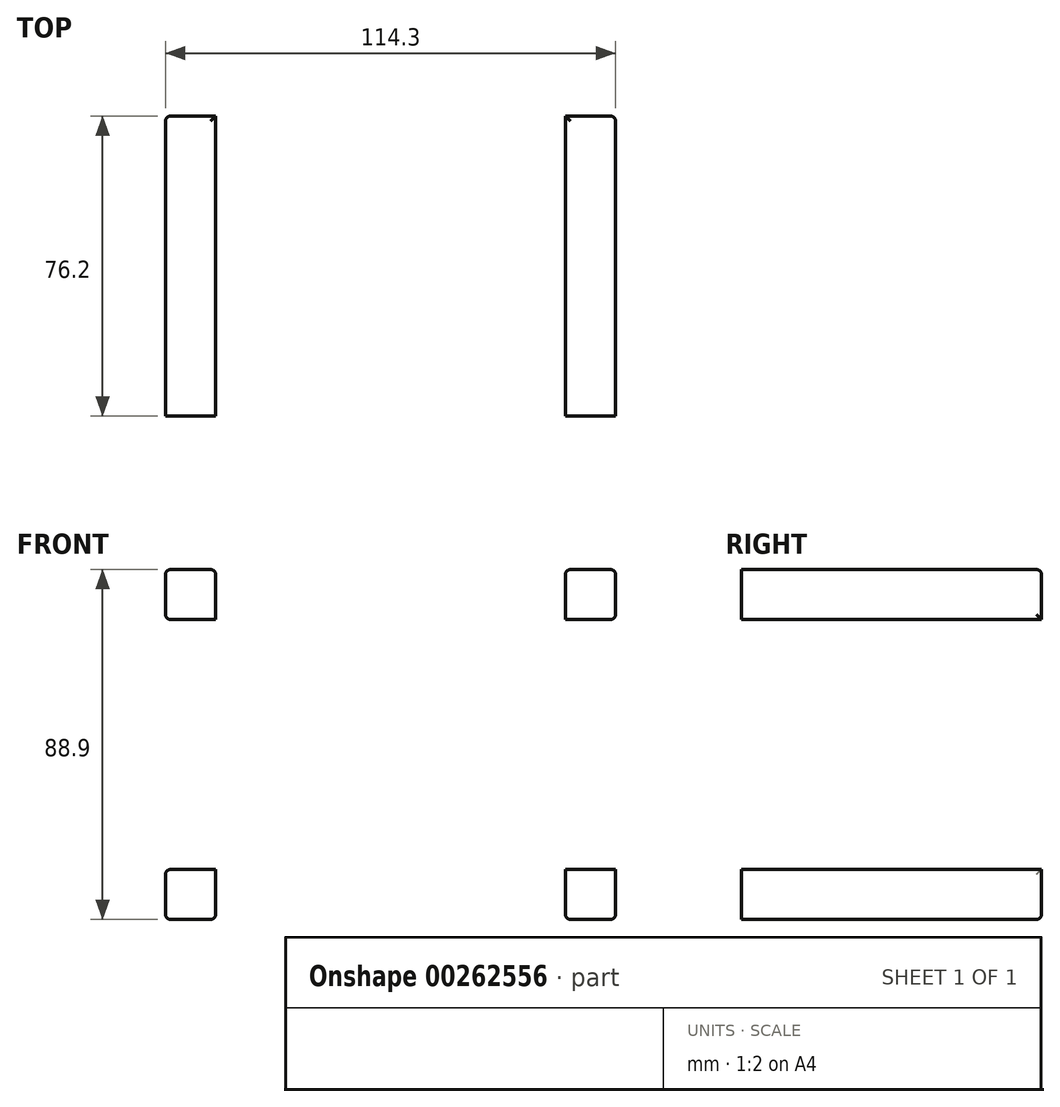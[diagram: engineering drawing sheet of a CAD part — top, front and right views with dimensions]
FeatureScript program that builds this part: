
annotation { "Feature Type Name" : "Feature", "Feature Type Description" : "" }
export const myFeature = defineFeature(function(context is Context, id is Id, definition is map)
    precondition{}
    {
        {
            var Q0;
            Q0=qCreatedBy(makeId("Front.planeOp"),FACE);
            var sketch = newSketch(context, id + "F0", { "sketchPlane" : qUnion([Q0])});
            skPoint(sketch, "E0.middle", {"position": v(0, 0) * mm});
            skLineSegment(sketch, "E1.bottom", {"start": v(-57.15, 44.45) * mm, "end": v(-44.45, 44.45) * mm});
            skLineSegment(sketch, "E1.top", {"start": v(-57.15, 31.75) * mm, "end": v(-44.45, 31.75) * mm});
            skLineSegment(sketch, "E1.left", {"start": v(-57.15, 44.45) * mm, "end": v(-57.15, 31.75) * mm});
            skLineSegment(sketch, "E1.right", {"start": v(-44.45, 44.45) * mm, "end": v(-44.45, 31.75) * mm});
            skPoint(sketch, "E1.middle", {"position": v(-50.8, 38.1) * mm});
            skLineSegment(sketch, "E2.bottom", {"start": v(-57.15, -44.45) * mm, "end": v(-44.45, -44.45) * mm});
            skLineSegment(sketch, "E2.top", {"start": v(-57.15, -31.75) * mm, "end": v(-44.45, -31.75) * mm});
            skLineSegment(sketch, "E2.left", {"start": v(-57.15, -44.45) * mm, "end": v(-57.15, -31.75) * mm});
            skLineSegment(sketch, "E2.right", {"start": v(-44.45, -44.45) * mm, "end": v(-44.45, -31.75) * mm});
            skPoint(sketch, "E2.middle", {"position": v(-50.8, -38.1) * mm});
            skLineSegment(sketch, "E3.bottom", {"start": v(57.15, -44.45) * mm, "end": v(44.45, -44.45) * mm});
            skLineSegment(sketch, "E3.top", {"start": v(57.15, -31.75) * mm, "end": v(44.45, -31.75) * mm});
            skLineSegment(sketch, "E3.left", {"start": v(57.15, -44.45) * mm, "end": v(57.15, -31.75) * mm});
            skLineSegment(sketch, "E3.right", {"start": v(44.45, -44.45) * mm, "end": v(44.45, -31.75) * mm});
            skPoint(sketch, "E3.middle", {"position": v(50.8, -38.1) * mm});
            skLineSegment(sketch, "E4.bottom", {"start": v(57.15, 44.45) * mm, "end": v(44.45, 44.45) * mm});
            skLineSegment(sketch, "E4.top", {"start": v(57.15, 31.75) * mm, "end": v(44.45, 31.75) * mm});
            skLineSegment(sketch, "E4.left", {"start": v(57.15, 44.45) * mm, "end": v(57.15, 31.75) * mm});
            skLineSegment(sketch, "E4.right", {"start": v(44.45, 44.45) * mm, "end": v(44.45, 31.75) * mm});
            skPoint(sketch, "E4.middle", {"position": v(50.8, 38.1) * mm});
            skSolve(sketch);
        }
        {
            var Q0;
            Q0 = qSketchRegion(id + "F0", true);
            extrude(context, id + "F1", {"entities" : qUnion([Q0]), "oppositeDirection" : true, "depth" : 76.2 * mm});
        }
        {
            var Q0;
            Q0=makeQuery(id+"F1.opExtrude","SWEPT_EDGE",EDGE,{"disambiguationData":[OSD([sQuery(id+"F0.wireOp",EDGE,"E1.bottom"),sQuery(id+"F0.wireOp",EDGE,"E1.left")])]});
            var Q1;
            Q1=makeQuery(id+"F1.opExtrude","SWEPT_EDGE",EDGE,{"disambiguationData":[OSD([sQuery(id+"F0.wireOp",EDGE,"E1.bottom"),sQuery(id+"F0.wireOp",EDGE,"E1.right")])]});
            var Q2;
            Q2=makeQuery(id+"F1.opExtrude","SWEPT_EDGE",EDGE,{"disambiguationData":[OSD([sQuery(id+"F0.wireOp",EDGE,"E4.bottom"),sQuery(id+"F0.wireOp",EDGE,"E4.left")])]});
            var Q3;
            Q3=makeQuery(id+"F1.opExtrude","SWEPT_EDGE",EDGE,{"disambiguationData":[OSD([sQuery(id+"F0.wireOp",EDGE,"E3.bottom"),sQuery(id+"F0.wireOp",EDGE,"E3.left")])]});
            var Q4;
            Q4=makeQuery(id+"F1.opExtrude","SWEPT_EDGE",EDGE,{"disambiguationData":[OSD([sQuery(id+"F0.wireOp",EDGE,"E4.top"),sQuery(id+"F0.wireOp",EDGE,"E4.left")])]});
            var Q5;
            Q5=makeQuery(id+"F1.opExtrude","SWEPT_EDGE",EDGE,{"disambiguationData":[OSD([sQuery(id+"F0.wireOp",EDGE,"E3.bottom"),sQuery(id+"F0.wireOp",EDGE,"E3.right")])]});
            var Q6;
            Q6=makeQuery(id+"F1.opExtrude","SWEPT_EDGE",EDGE,{"disambiguationData":[OSD([sQuery(id+"F0.wireOp",EDGE,"E2.bottom"),sQuery(id+"F0.wireOp",EDGE,"E2.left")])]});
            var Q7;
            Q7=makeQuery(id+"F1.opExtrude","SWEPT_EDGE",EDGE,{"disambiguationData":[OSD([sQuery(id+"F0.wireOp",EDGE,"E1.top"),sQuery(id+"F0.wireOp",EDGE,"E1.left")])]});
            var Q8;
            Q8=makeQuery(id+"F1.opExtrude","CAP_EDGE",EDGE,{"disambiguationData":[OSD([sQuery(id+"F0.wireOp",EDGE,"E2.bottom")])],"isStart":false});
            var Q9;
            Q9=makeQuery(id+"F1.opExtrude","CAP_EDGE",EDGE,{"disambiguationData":[OSD([sQuery(id+"F0.wireOp",EDGE,"E1.left")])],"isStart":false});
            var Q10;
            Q10=makeQuery(id+"F1.opExtrude","CAP_EDGE",EDGE,{"disambiguationData":[OSD([sQuery(id+"F0.wireOp",EDGE,"E3.bottom")])],"isStart":false});
            var Q11;
            Q11=makeQuery(id+"F1.opExtrude","CAP_EDGE",EDGE,{"disambiguationData":[OSD([sQuery(id+"F0.wireOp",EDGE,"E1.bottom")])],"isStart":false});
            var Q12;
            Q12=makeQuery(id+"F1.opExtrude","CAP_EDGE",EDGE,{"disambiguationData":[OSD([sQuery(id+"F0.wireOp",EDGE,"E4.bottom")])],"isStart":false});
            var Q13;
            Q13=makeQuery(id+"F1.opExtrude","SWEPT_EDGE",EDGE,{"disambiguationData":[OSD([sQuery(id+"F0.wireOp",EDGE,"E4.bottom"),sQuery(id+"F0.wireOp",EDGE,"E4.right")])]});
            var Q14;
            Q14=makeQuery(id+"F1.opExtrude","CAP_EDGE",EDGE,{"disambiguationData":[OSD([sQuery(id+"F0.wireOp",EDGE,"E4.left")])],"isStart":false});
            var Q15;
            Q15=makeQuery(id+"F1.opExtrude","CAP_EDGE",EDGE,{"disambiguationData":[OSD([sQuery(id+"F0.wireOp",EDGE,"E3.left")])],"isStart":false});
            var Q16;
            Q16=makeQuery(id+"F1.opExtrude","CAP_EDGE",EDGE,{"disambiguationData":[OSD([sQuery(id+"F0.wireOp",EDGE,"E2.left")])],"isStart":false});
            var Q17;
            Q17=makeQuery(id+"F1.opExtrude","SWEPT_EDGE",EDGE,{"disambiguationData":[OSD([sQuery(id+"F0.wireOp",EDGE,"E2.top"),sQuery(id+"F0.wireOp",EDGE,"E2.left")])]});
            var Q18;
            Q18=makeQuery(id+"F1.opExtrude","SWEPT_EDGE",EDGE,{"disambiguationData":[OSD([sQuery(id+"F0.wireOp",EDGE,"E2.bottom"),sQuery(id+"F0.wireOp",EDGE,"E2.right")])]});
            fillet(context, id + "F2", {"entities" : qUnion([Q0, Q1, Q2, Q3, Q4, Q5, Q6, Q7, Q8, Q9, Q10, Q11, Q12, Q13, Q14, Q15, Q16, Q17, Q18]), "radius" : 1.27 * mm, "tangentPropagation" : true, "allowEdgeOverflow" : false});
        }
    });
